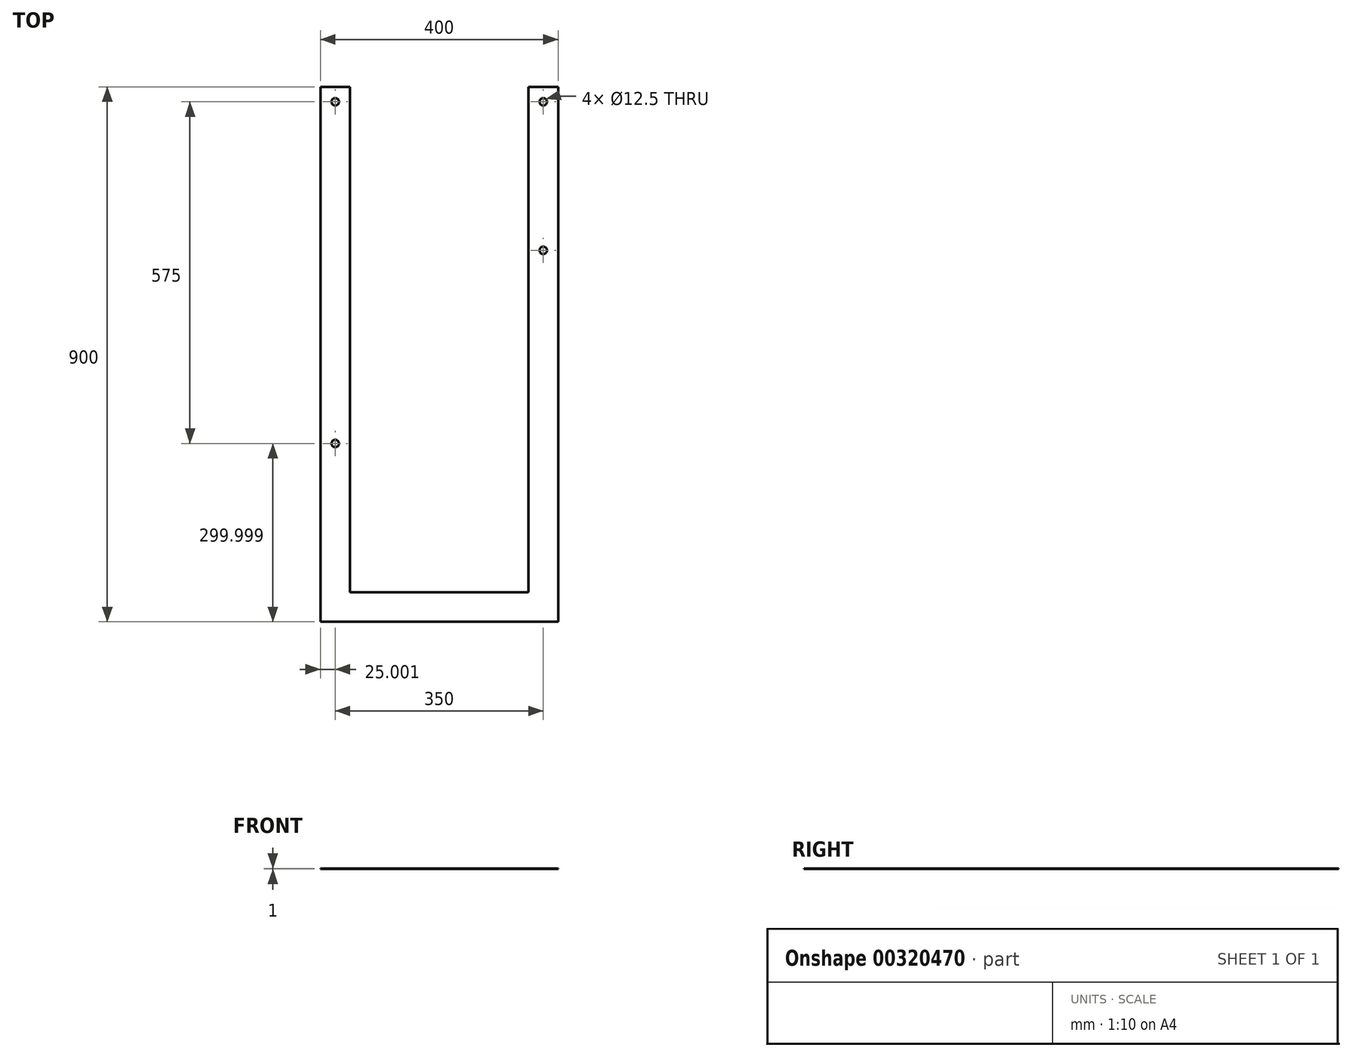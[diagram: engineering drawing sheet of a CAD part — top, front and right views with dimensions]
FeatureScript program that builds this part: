
annotation { "Feature Type Name" : "Feature", "Feature Type Description" : "" }
export const myFeature = defineFeature(function(context is Context, id is Id, definition is map)
    precondition{}
    {
        {
            var Q0;
            Q0=qCreatedBy(makeId("Top.planeOp"),FACE);
            var sketch = newSketch(context, id + "F0", { "sketchPlane" : qUnion([Q0])});
            skLineSegment(sketch, "E0", {"start": v(-123.53, -335.98) * mm, "end": v(-173.53, -335.98) * mm});
            skLineSegment(sketch, "E1", {"start": v(-173.53, -335.98) * mm, "end": v(-173.53, 564.02) * mm});
            skLineSegment(sketch, "E2", {"start": v(226.47, 564.02) * mm, "end": v(226.47, -335.98) * mm});
            skLineSegment(sketch, "E3", {"start": v(226.47, -335.98) * mm, "end": v(176.47, -335.98) * mm});
            skLineSegment(sketch, "E4", {"start": v(176.47, -285.98) * mm, "end": v(176.47, 513.96) * mm});
            skLineSegment(sketch, "E5", {"start": v(-123.53, 513.96) * mm, "end": v(-123.53, -285.98) * mm});
            skCircle(sketch, "E6", {"center": v(-148.53, 539.02) * mm, "radius": 6.25 * mm});
            skCircle(sketch, "E7", {"center": v(-148.53, -35.98) * mm, "radius": 6.25 * mm});
            skCircle(sketch, "E8.MirrorC", {"center": v(201.47, 539.02) * mm, "radius": 6.25 * mm});
            skCircle(sketch, "E9", {"center": v(201.47, 289.02) * mm, "radius": 6.25 * mm});
            skLineSegment(sketch, "E10", {"start": v(-173.53, 564.02) * mm, "end": v(-123.53, 564.02) * mm});
            skLineSegment(sketch, "E11", {"start": v(-123.53, 564.02) * mm, "end": v(-123.53, 513.96) * mm});
            skLineSegment(sketch, "E12", {"start": v(226.47, 564.02) * mm, "end": v(176.47, 564.02) * mm});
            skLineSegment(sketch, "E13", {"start": v(176.47, 564.02) * mm, "end": v(176.47, 513.96) * mm});
            skLineSegment(sketch, "E14", {"start": v(-123.53, -335.98) * mm, "end": v(176.47, -335.98) * mm});
            skLineSegment(sketch, "E15", {"start": v(-123.53, -285.98) * mm, "end": v(176.47, -285.98) * mm});
            skSolve(sketch);
        }
        {
            var Q0;
            Q0 = qSketchRegion(id + "F0", true);
            extrude(context, id + "F1", {"entities" : qUnion([Q0]), "depth" : 1 * mm});
        }
    });
